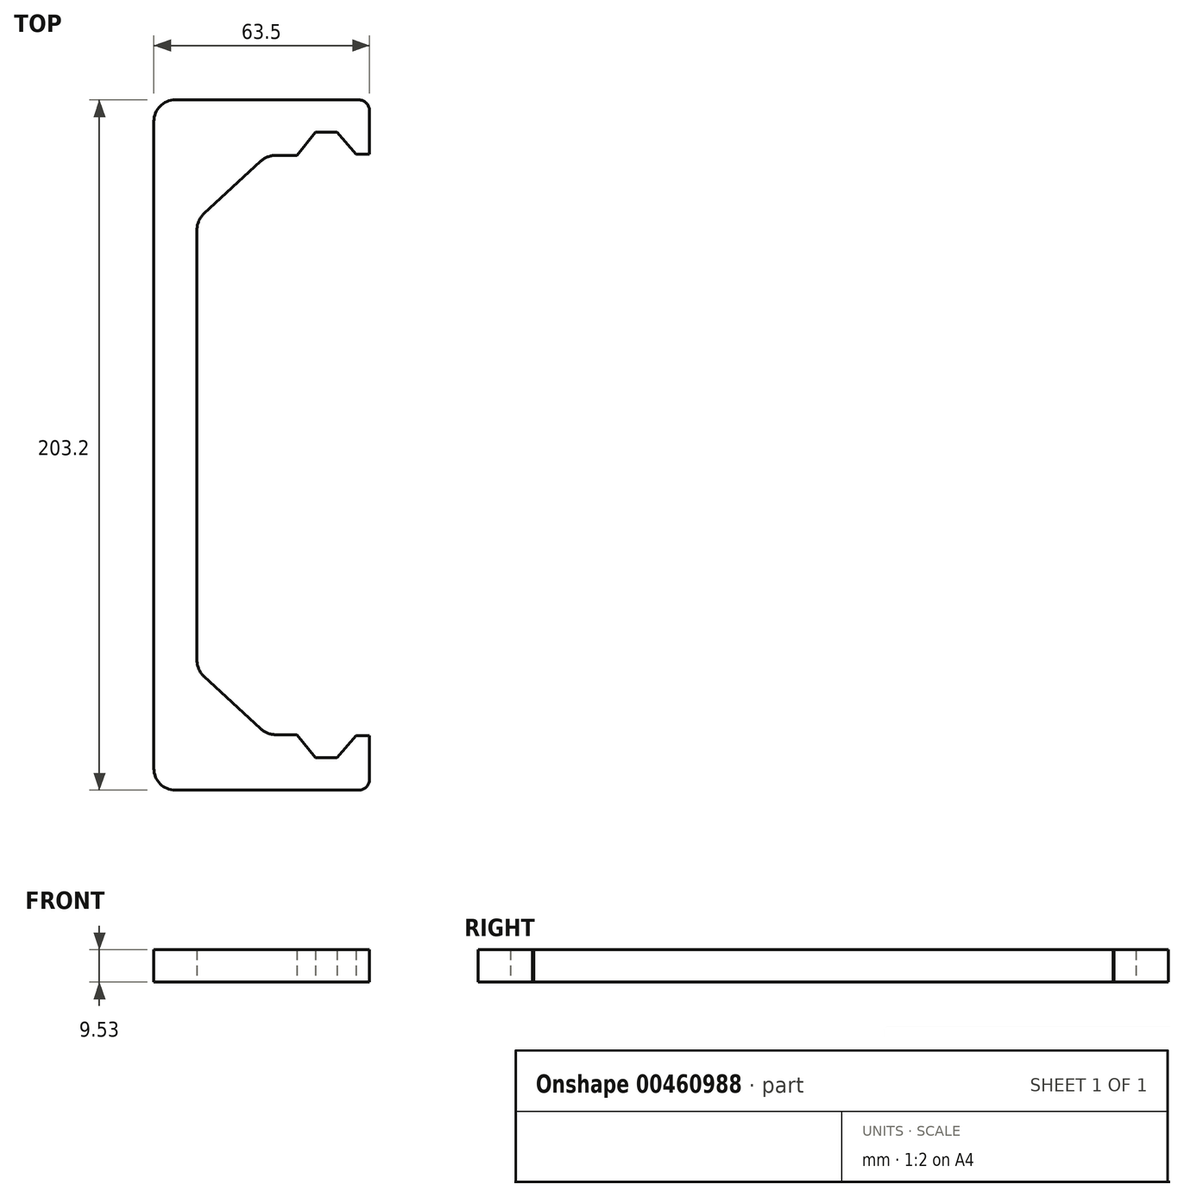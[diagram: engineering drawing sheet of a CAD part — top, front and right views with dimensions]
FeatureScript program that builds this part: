
annotation { "Feature Type Name" : "Feature", "Feature Type Description" : "" }
export const myFeature = defineFeature(function(context is Context, id is Id, definition is map)
    precondition{}
    {
        {
            var Q0;
            Q0=qCreatedBy(makeId("Top.planeOp"),FACE);
            var sketch = newSketch(context, id + "F0", { "sketchPlane" : qUnion([Q0])});
            skLineSegment(sketch, "E0.bottom", {"start": v(-46.74, 147.98) * mm, "end": v(-2.29, 147.98) * mm});
            skLineSegment(sketch, "E0.top", {"start": v(-46.74, -55.22) * mm, "end": v(-2.29, -55.22) * mm});
            skLineSegment(sketch, "E0.left", {"start": v(-53.09, 141.63) * mm, "end": v(-53.09, -48.87) * mm});
            skLineSegment(sketch, "E1.0", {"start": v(-40.39, 109.8) * mm, "end": v(-40.39, -17.05) * mm});
            skPoint(sketch, "E2.orphan", {"position": v(-2.29, 147.98) * mm});
            skPoint(sketch, "E3.visualSharp", {"position": v(-53.09, 147.98) * mm});
            skArc(sketch, "E3.filletArc", {"start": v(-46.74, 147.98) * mm, "mid": v(-51.23, 146.12) * mm, "end": v(-53.09, 141.63) * mm});
            skArc(sketch, "E4.filletArc", {"start": v(-53.09, -48.87) * mm, "mid": v(-51.23, -53.36) * mm, "end": v(-46.74, -55.22) * mm});
            skPoint(sketch, "E5.orphan", {"position": v(10.41, 147.98) * mm});
            skPoint(sketch, "E6.start.orphan", {"position": v(-53.09, 46.38) * mm});
            skLineSegment(sketch, "E7", {"start": v(-2.29, 147.98) * mm, "end": v(7.24, 147.98) * mm});
            skLineSegment(sketch, "E8.MirrorCS", {"start": v(-2.29, -55.22) * mm, "end": v(7.24, -55.22) * mm});
            skLineSegment(sketch, "E9", {"start": v(10.41, 144.8) * mm, "end": v(10.41, 131.98) * mm});
            skLineSegment(sketch, "E10", {"start": v(6.43, 131.98) * mm, "end": v(0.89, 138.45) * mm});
            skLineSegment(sketch, "E11", {"start": v(0.89, 138.45) * mm, "end": v(-5.46, 138.45) * mm});
            skLineSegment(sketch, "E12", {"start": v(-5.46, 138.45) * mm, "end": v(-11, 131.64) * mm});
            skLineSegment(sketch, "E13", {"start": v(-11, 131.64) * mm, "end": v(-17.27, 131.64) * mm});
            skLineSegment(sketch, "E14", {"start": v(-21.57, 129.96) * mm, "end": v(-38.34, 114.48) * mm});
            skLineSegment(sketch, "E15", {"start": v(6.43, 131.98) * mm, "end": v(10.41, 131.98) * mm});
            skLineSegment(sketch, "E16.MirrorCS", {"start": v(10.41, -52.05) * mm, "end": v(10.41, -39.22) * mm});
            skLineSegment(sketch, "E17.MirrorCS", {"start": v(6.43, -39.22) * mm, "end": v(10.41, -39.22) * mm});
            skLineSegment(sketch, "E18.MirrorCS", {"start": v(6.43, -39.22) * mm, "end": v(0.89, -45.7) * mm});
            skLineSegment(sketch, "E19.MirrorCS", {"start": v(0.89, -45.7) * mm, "end": v(-5.46, -45.7) * mm});
            skLineSegment(sketch, "E20.MirrorCS", {"start": v(-5.46, -45.7) * mm, "end": v(-11, -38.88) * mm});
            skLineSegment(sketch, "E21.MirrorCS", {"start": v(-11, -38.88) * mm, "end": v(-17.27, -38.88) * mm});
            skLineSegment(sketch, "E22.MirrorCS", {"start": v(-21.57, -37.2) * mm, "end": v(-38.34, -21.72) * mm});
            skPoint(sketch, "E23.visualSharp", {"position": v(-19.75, 131.64) * mm});
            skArc(sketch, "E23.filletArc", {"start": v(-17.27, 131.64) * mm, "mid": v(-19.58, 131.2) * mm, "end": v(-21.57, 129.96) * mm});
            skPoint(sketch, "E24.visualSharp", {"position": v(-40.39, 112.59) * mm});
            skArc(sketch, "E24.filletArc", {"start": v(-38.34, 114.48) * mm, "mid": v(-39.85, 112.36) * mm, "end": v(-40.39, 109.8) * mm});
            skPoint(sketch, "E25.visualSharp", {"position": v(-40.39, -19.83) * mm});
            skArc(sketch, "E25.filletArc", {"start": v(-40.39, -17.05) * mm, "mid": v(-39.85, -19.6) * mm, "end": v(-38.34, -21.72) * mm});
            skPoint(sketch, "E26.visualSharp", {"position": v(-19.75, -38.88) * mm});
            skArc(sketch, "E26.filletArc", {"start": v(-21.57, -37.2) * mm, "mid": v(-19.58, -38.44) * mm, "end": v(-17.27, -38.88) * mm});
            skPoint(sketch, "E27.visualSharp", {"position": v(10.41, -55.22) * mm});
            skArc(sketch, "E27.filletArc", {"start": v(7.24, -55.22) * mm, "mid": v(9.48, -54.3) * mm, "end": v(10.41, -52.05) * mm});
            skArc(sketch, "E28.filletArc", {"start": v(10.41, 144.8) * mm, "mid": v(9.48, 147.05) * mm, "end": v(7.24, 147.98) * mm});
            skSolve(sketch);
        }
        {
            var Q0;
            Q0=makeQuery(id+"F0.imprint","IMPRINT",FACE,{"disambiguationData":[TD([[makeQuery(id+"F0.imprint","IMPRINT",EDGE,{"derivedFrom":sQuery(id+"F0.wireOp",EDGE,"E0.bottom")}),-1.0]])]});
            var Q1;
            Q1=makeQuery(id+"F0.imprint","IMPRINT",FACE,{"disambiguationData":[TD([[makeQuery(id+"F0.imprint","IMPRINT",EDGE,{"derivedFrom":sQuery(id+"F0.wireOp",EDGE,"E0.top")}),1.0]])]});
            extrude(context, id + "F1", {"entities" : qUnion([Q0, Q1]), "depth" : 9.52 * mm, "offsetDistance" : 25.4 * mm});
        }
    });
